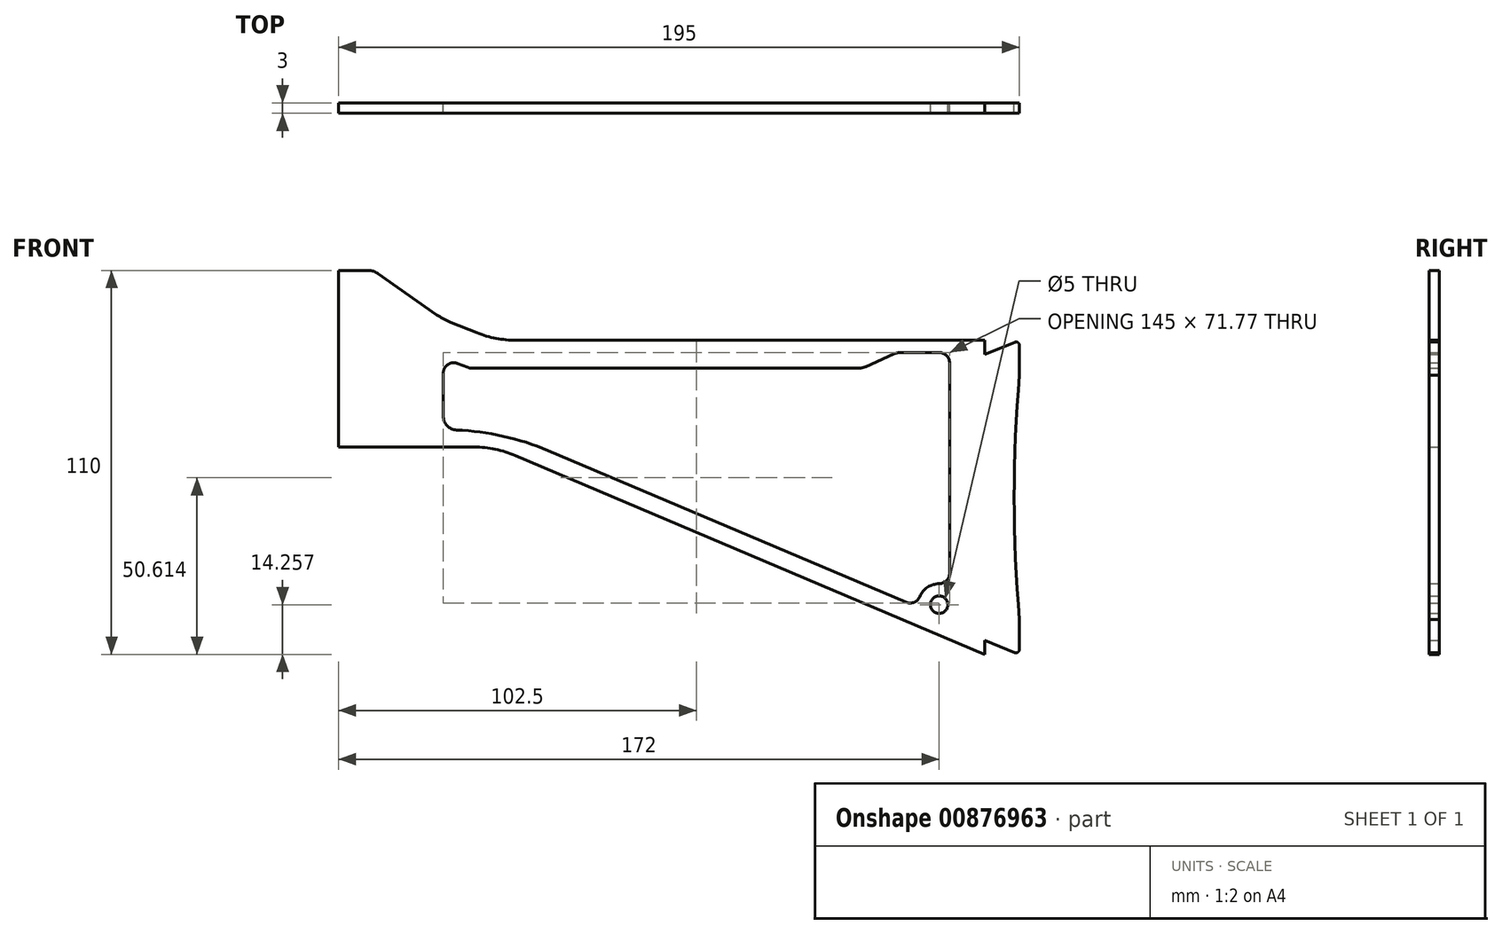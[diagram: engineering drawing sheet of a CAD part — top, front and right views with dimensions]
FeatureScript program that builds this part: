
annotation { "Feature Type Name" : "Feature", "Feature Type Description" : "" }
export const myFeature = defineFeature(function(context is Context, id is Id, definition is map)
    precondition{}
    {
        {
            var Q0;
            Q0=qCreatedBy(makeId("Front.planeOp"),FACE);
            var sketch = newSketch(context, id + "F0", { "sketchPlane" : qUnion([Q0])});
            skLineSegment(sketch, "E0", {"start": v(0, 0) * mm, "end": v(0, -50.6) * mm});
            skLineSegment(sketch, "E1", {"start": v(0, 0) * mm, "end": v(8.42, 0) * mm});
            skLineSegment(sketch, "E2", {"start": v(11.3, -0.9) * mm, "end": v(28.1, -12.68) * mm});
            skLineSegment(sketch, "E3", {"start": v(32.15, -14.86) * mm, "end": v(39.64, -17.86) * mm});
            skLineSegment(sketch, "E4", {"start": v(50.77, -20) * mm, "end": v(185, -20) * mm});
            skLineSegment(sketch, "E5", {"start": v(185, -20) * mm, "end": v(185, -24) * mm});
            skLineSegment(sketch, "E6", {"start": v(185, -24) * mm, "end": v(193.63, -20.55) * mm});
            skLineSegment(sketch, "E7", {"start": v(195, -21.48) * mm, "end": v(195, -30) * mm});
            skLineSegment(sketch, "E8", {"start": v(0, -50.6) * mm, "end": v(38.9, -50.6) * mm});
            skLineSegment(sketch, "E9", {"start": v(50.62, -53) * mm, "end": v(185, -110) * mm});
            skLineSegment(sketch, "E10", {"start": v(185, -110) * mm, "end": v(185, -106) * mm});
            skLineSegment(sketch, "E11", {"start": v(185, -106) * mm, "end": v(193.63, -109.45) * mm});
            skLineSegment(sketch, "E12", {"start": v(195, -108.52) * mm, "end": v(195, -100) * mm});
            skArc(sketch, "E13", {"start": v(195, -30) * mm, "mid": v(193.47, -65) * mm, "end": v(195, -100) * mm});
            skPoint(sketch, "E14.visualSharp", {"position": v(10, 0) * mm});
            skArc(sketch, "E14.filletArc", {"start": v(11.3, -0.9) * mm, "mid": v(9.93, -0.23) * mm, "end": v(8.42, 0) * mm});
            skPoint(sketch, "E15.visualSharp", {"position": v(30, -14) * mm});
            skArc(sketch, "E15.filletArc", {"start": v(28.1, -12.68) * mm, "mid": v(30.06, -13.89) * mm, "end": v(32.15, -14.86) * mm});
            skPoint(sketch, "E16.visualSharp", {"position": v(45, -20) * mm});
            skArc(sketch, "E16.filletArc", {"start": v(39.64, -17.86) * mm, "mid": v(45.1, -19.46) * mm, "end": v(50.77, -20) * mm});
            skPoint(sketch, "E17.visualSharp", {"position": v(45, -50.6) * mm});
            skArc(sketch, "E17.filletArc", {"start": v(50.62, -53) * mm, "mid": v(44.88, -51.21) * mm, "end": v(38.9, -50.6) * mm});
            skPoint(sketch, "E18.visualSharp", {"position": v(195, -20) * mm});
            skArc(sketch, "E18.filletArc", {"start": v(195, -21.48) * mm, "mid": v(194.56, -20.65) * mm, "end": v(193.63, -20.55) * mm});
            skPoint(sketch, "E19.visualSharp", {"position": v(195, -110) * mm});
            skArc(sketch, "E19.filletArc", {"start": v(193.63, -109.45) * mm, "mid": v(194.56, -109.35) * mm, "end": v(195, -108.52) * mm});
            skPoint(sketch, "E20.visualSharp", {"position": v(60.02, -51.55) * mm});
            skPoint(sketch, "E21", {"position": v(30, -45.6) * mm});
            skArc(sketch, "E22", {"start": v(33.81, -45.7) * mm, "mid": v(47.17, -47.5) * mm, "end": v(60.02, -51.55) * mm});
            skLineSegment(sketch, "E23", {"start": v(30, -41.7) * mm, "end": v(30, -29.43) * mm});
            skPoint(sketch, "E24", {"position": v(37.5, -28) * mm});
            skLineSegment(sketch, "E25", {"start": v(34.11, -26.64) * mm, "end": v(36.97, -27.79) * mm});
            skPoint(sketch, "E26", {"position": v(150, -28) * mm});
            skLineSegment(sketch, "E27", {"start": v(150.98, -27.56) * mm, "end": v(159.02, -23.94) * mm});
            skLineSegment(sketch, "E28", {"start": v(148.93, -28) * mm, "end": v(38.08, -28) * mm});
            skPoint(sketch, "E29.visualSharp", {"position": v(160, -23.5) * mm});
            skArc(sketch, "E29.filletArc", {"start": v(161.07, -23.5) * mm, "mid": v(160.02, -23.61) * mm, "end": v(159.02, -23.94) * mm});
            skArc(sketch, "E30.filletArc", {"start": v(148.93, -28) * mm, "mid": v(149.98, -27.89) * mm, "end": v(150.98, -27.56) * mm});
            skArc(sketch, "E31.filletArc", {"start": v(30, -41.7) * mm, "mid": v(31.1, -44.46) * mm, "end": v(33.81, -45.7) * mm});
            skPoint(sketch, "E32.visualSharp", {"position": v(30, -25) * mm});
            skArc(sketch, "E32.filletArc", {"start": v(34.11, -26.64) * mm, "mid": v(31.32, -26.95) * mm, "end": v(30, -29.43) * mm});
            skArc(sketch, "E33.filletArc", {"start": v(36.97, -27.79) * mm, "mid": v(37.52, -27.95) * mm, "end": v(38.08, -28) * mm});
            skPoint(sketch, "E34", {"position": v(172, -95.74) * mm});
            skCircle(sketch, "E35", {"center": v(172, -95.74) * mm, "radius": 2.5 * mm});
            skLineSegment(sketch, "E36", {"start": v(60.02, -51.55) * mm, "end": v(162.52, -95.03) * mm});
            skLineSegment(sketch, "E37", {"start": v(175, -86.74) * mm, "end": v(175, -26.5) * mm});
            skLineSegment(sketch, "E38", {"start": v(161.07, -23.5) * mm, "end": v(172, -23.5) * mm});
            skPoint(sketch, "E39.visualSharp", {"position": v(175, -23.5) * mm});
            skArc(sketch, "E39.filletArc", {"start": v(175, -26.5) * mm, "mid": v(174.12, -24.38) * mm, "end": v(172, -23.5) * mm});
            skArc(sketch, "E40", {"start": v(166.46, -93.43) * mm, "mid": v(168.67, -90.75) * mm, "end": v(172, -89.74) * mm});
            skPoint(sketch, "E41.visualSharp", {"position": v(166.05, -96.53) * mm});
            skArc(sketch, "E41.filletArc", {"start": v(162.52, -95.03) * mm, "mid": v(164.83, -95.05) * mm, "end": v(166.46, -93.43) * mm});
            skPoint(sketch, "E42.visualSharp", {"position": v(175, -90.55) * mm});
            skArc(sketch, "E42.filletArc", {"start": v(172, -89.74) * mm, "mid": v(174.12, -88.86) * mm, "end": v(175, -86.74) * mm});
            skSolve(sketch);
        }
        {
            var Q0;
            Q0=makeQuery(id+"F0.imprint","IMPRINT",FACE,{"disambiguationData":[TD([[makeQuery(id+"F0.imprint","IMPRINT",EDGE,{"derivedFrom":sQuery(id+"F0.wireOp",EDGE,"E0")}),1.0]])]});
            extrude(context, id + "F1", {"entities" : qUnion([Q0]), "depth" : 3 * mm, "offsetDistance" : 25 * mm});
        }
    });
